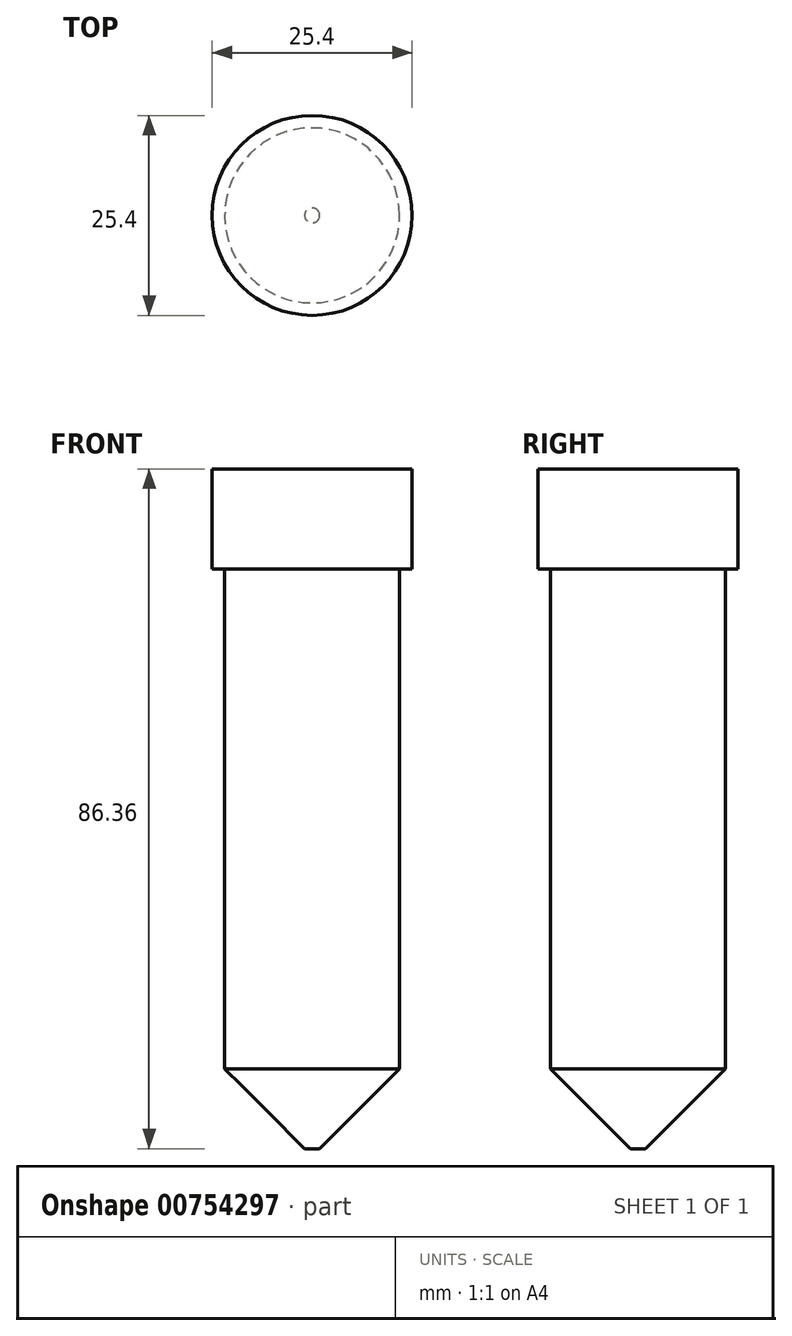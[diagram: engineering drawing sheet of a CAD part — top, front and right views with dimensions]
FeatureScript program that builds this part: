
annotation { "Feature Type Name" : "Feature", "Feature Type Description" : "" }
export const myFeature = defineFeature(function(context is Context, id is Id, definition is map)
    precondition{}
    {
        {
            var Q0;
            Q0=qCreatedBy(makeId("Top.planeOp"),FACE);
            var sketch = newSketch(context, id + "F0", { "sketchPlane" : qUnion([Q0])});
            skCircle(sketch, "E0", {"center": v(0, 0) * mm, "radius": 12.7 * mm});
            skSolve(sketch);
        }
        {
            var Q0;
            Q0=makeQuery(id+"F0.imprint","IMPRINT",FACE,{"disambiguationData":[TD([[makeQuery(id+"F0.imprint","IMPRINT",EDGE,{"derivedFrom":sQuery(id+"F0.wireOp",EDGE,"E0")}),1.0]])]});
            extrude(context, id + "F1", {"entities" : qUnion([Q0]), "oppositeDirection" : true, "depth" : 12.7 * mm, "offsetDistance" : 25.4 * mm});
        }
        {
            var Q0;
            Q0=makeQuery(id+"F1.opExtrude","CAP_FACE",FACE,{"disambiguationData":[OSD([sQuery(id+"F0.wireOp",EDGE,"E0")])],"isStart":false});
            var sketch = newSketch(context, id + "F2", { "sketchPlane" : qUnion([Q0])});
            skCircle(sketch, "E1", {"center": v(0, 0) * mm, "radius": 11.11 * mm});
            skSolve(sketch);
        }
        {
            var Q0;
            Q0=makeQuery(id+"F2.imprint","IMPRINT",FACE,{"disambiguationData":[TD([[makeQuery(id+"F2.imprint","IMPRINT",EDGE,{"derivedFrom":sQuery(id+"F2.wireOp",EDGE,"E1")}),1.0]])]});
            extrude(context, id + "F3", {"entities" : qUnion([Q0]), "operationType" : NewBodyOperationType.ADD, "depth" : 63.5 * mm, "offsetDistance" : 25.4 * mm});
        }
        {
            var Q0;
            Q0=makeQuery(id+"F3.opExtrude","CAP_FACE",FACE,{"disambiguationData":[OSD([sQuery(id+"F2.wireOp",EDGE,"E1")])],"isStart":false});
            var sketch = newSketch(context, id + "F4", { "sketchPlane" : qUnion([Q0])});
            skCircle(sketch, "E2", {"center": v(0, 0) * mm, "radius": 11.11 * mm});
            skSolve(sketch);
        }
        {
            var Q0;
            Q0=makeQuery(id+"F4.imprint","IMPRINT",FACE,{"disambiguationData":[TD([[makeQuery(id+"F4.imprint","IMPRINT",EDGE,{"derivedFrom":sQuery(id+"F4.wireOp",EDGE,"E2")}),1.0]])]});
            extrude(context, id + "F5", {"entities" : qUnion([Q0]), "operationType" : NewBodyOperationType.ADD, "depth" : 10.16 * mm, "offsetDistance" : 25.4 * mm, "hasDraft" : true, "draftAngle" : 45 * degree, "draftPullDirection" : true});
        }
    });
